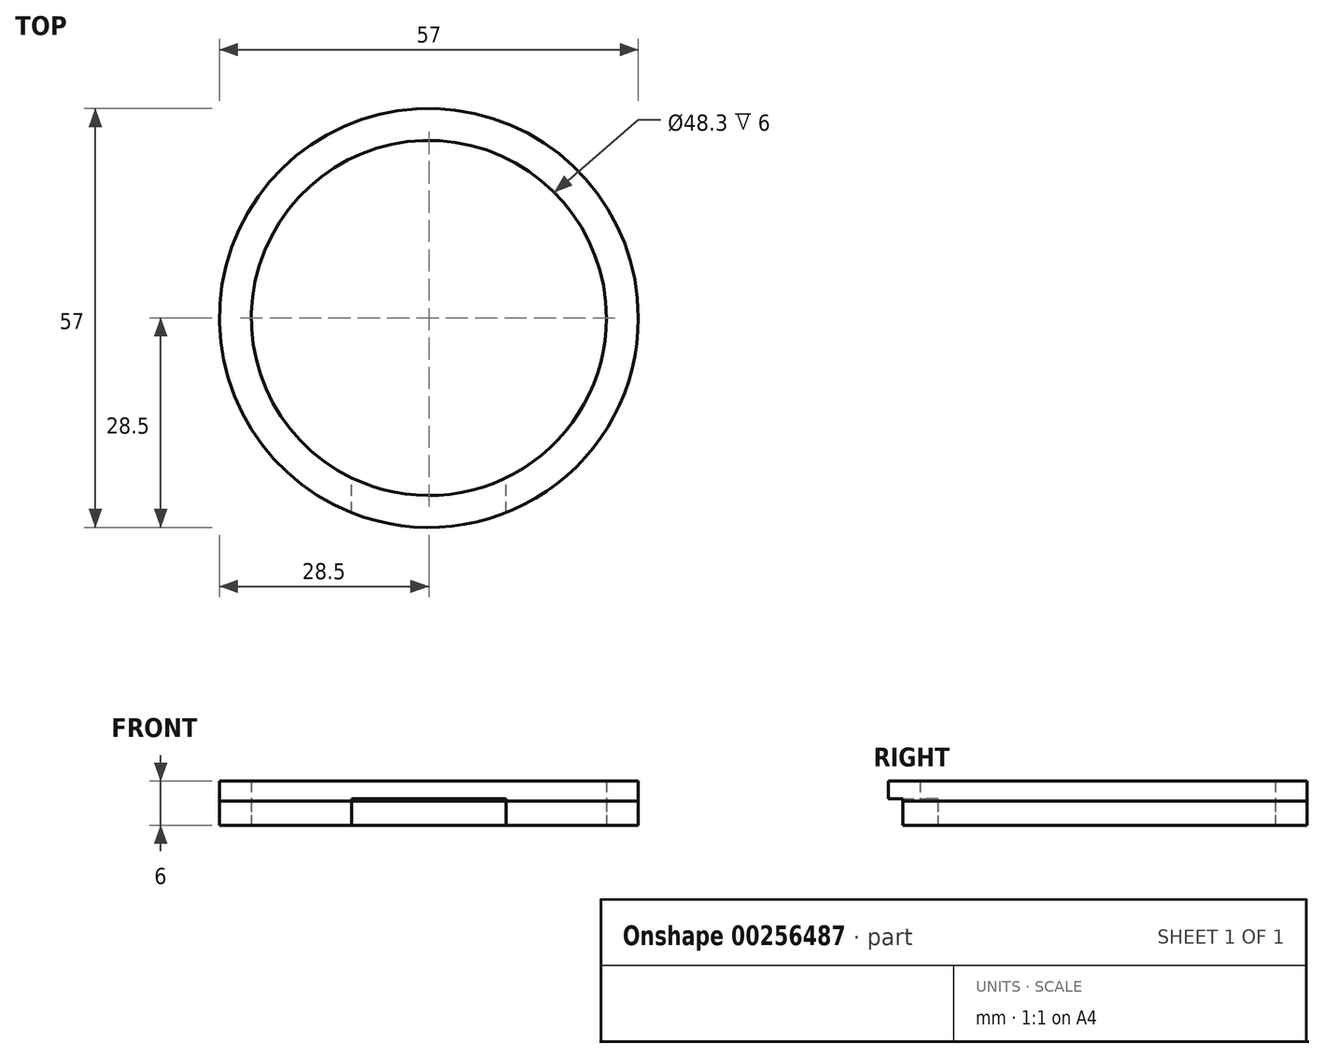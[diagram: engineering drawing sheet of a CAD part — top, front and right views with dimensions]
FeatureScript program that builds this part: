
annotation { "Feature Type Name" : "Feature", "Feature Type Description" : "" }
export const myFeature = defineFeature(function(context is Context, id is Id, definition is map)
    precondition{}
    {
        {
            var Q0;
            Q0=qCreatedBy(makeId("Top.planeOp"),FACE);
            var sketch = newSketch(context, id + "F0", { "sketchPlane" : qUnion([Q0])});
            skCircle(sketch, "E0", {"center": v(0, 0) * mm, "radius": 8.05 * mm});
            skCircle(sketch, "E1", {"center": v(0, 0) * mm, "radius": 9.5 * mm});
            skSolve(sketch);
        }
        {
            var Q0;
            Q0=makeQuery(id+"F0.imprint","IMPRINT",FACE,{"disambiguationData":[TD([[makeQuery(id+"F0.imprint","IMPRINT",EDGE,{"derivedFrom":sQuery(id+"F0.wireOp",EDGE,"E0")}),-1.0]])]});
            extrude(context, id + "F1", {"entities" : qUnion([Q0]), "depth" : 1.1 * mm});
        }
        {
            var Q0;
            Q0=makeQuery(id+"F0.imprint","IMPRINT",FACE,{"disambiguationData":[TD([[makeQuery(id+"F0.imprint","IMPRINT",EDGE,{"derivedFrom":sQuery(id+"F0.wireOp",EDGE,"E0")}),-1.0]])]});
            extrude(context, id + "F2", {"entities" : qUnion([Q0]), "depth" : 2 * mm});
        }
        {
            var Q0;
            Q0=makeQuery(id+"F2.opExtrude","CAP_FACE",FACE,{"disambiguationData":[OSD([sQuery(id+"F0.wireOp",EDGE,"E0"),sQuery(id+"F0.wireOp",EDGE,"E1")])],"isStart":true});
            var sketch = newSketch(context, id + "F3", { "sketchPlane" : qUnion([Q0])});
            skLineSegment(sketch, "E2", {"start": v(-3.5, 8.83) * mm, "end": v(-3.5, 7.25) * mm});
            skLineSegment(sketch, "E3", {"start": v(3.5, 8.83) * mm, "end": v(3.5, 7.25) * mm});
            skSolve(sketch);
        }
        {
            var Q0;
            {var subQ2=sQuery(id+"F3.wireOp",EDGE,"E2");Q0=makeQuery(id+"F3.imprint","IMPRINT",FACE,{"disambiguationData":[TD([[makeQuery(id+"F3.imprint","IMPRINT",EDGE,{"derivedFrom":subQ2}),1.0]])]});}
            extrude(context, id + "F4", {"entities" : qUnion([Q0]), "operationType" : NewBodyOperationType.REMOVE, "oppositeDirection" : true, "depth" : 1.2 * mm});
        }
        {
            var Q0;
            Q0=makeQuery(id+"F1.opExtrude","SWEPT_BODY",BODY,{"disambiguationData":[OSD([sQuery(id+"F0.wireOp",EDGE,"E0"),sQuery(id+"F0.wireOp",EDGE,"E1")])]});
            var Q1;
            Q1=makeQuery(id+"F2.opExtrude","SWEPT_BODY",BODY,{"disambiguationData":[OSD([sQuery(id+"F0.wireOp",EDGE,"E0"),sQuery(id+"F0.wireOp",EDGE,"E1")])]});
            var Q2;
            Q2=qCreatedBy(makeId("Origin.pointOp"),VERTEX);
            transform(context, id + "F5", {"entities" : qUnion([Q0, Q1]), "transformType" : TransformType.SCALE_UNIFORMLY, "scale" : 3, "makeCopy" : false, "scalePoint" : qUnion([Q2])});
        }
    });
